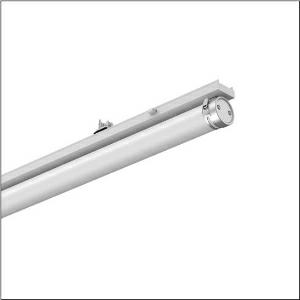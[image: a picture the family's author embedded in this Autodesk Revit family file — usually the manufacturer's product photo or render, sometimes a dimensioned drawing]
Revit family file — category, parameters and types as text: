
# Revit family: monsun_r__31_tube_51ft10nn4a0atr1_e6cc
name_source: partatom
category: Lighting Fixtures
units: mm (PartAtom-declared; Revit-internal decimal feet)

## family parameters
Cut with Voids When Loaded = No
Host = Face
Light Source = No
Part Type = Normal
Room Calculation Point = No
Round Connector Dimension = Use Diameter
Shared = No

## types (1)
- --- (1 x LED, 10000 lm, 58 W, 4000K)
    Apparent Load = 58 VA
    CIE Flux Codes = 42 71 90 91 100
    Color Rendering = 80
    Color Temperature = 4000K
    Default Elevation = 1800 mm
    Description = Monsun® 31 Tube, tubular luminaire, primary optical cover: diffuser, of PMMA, light emission: direct distribution, primary light characteristic: symmetric, LED, rated luminous flux: 10.000lm, luminous efficacy: 172lm/W, light colour: 840, colour temperature: 4000K, control gear: DALI Multilumen, with with 1 terminal, 5-pole, max. 2.5mm², mains connection: 220..240V, AC, 50/60Hz, rated input power: 58W, housing, cylindrical, of PMMA, semi-transparent, matt white, with luminaire and ceiling fastening, V4A, mounting with brackets of stainless steel, length: 1.495mm, diameter: 75mm, end cap, of stainless steel (V4A), protection rating (complete): IP20, protection rating (lamp compartment): IP67/69K, insulation class (complete): insulation class I (protective earthing), certification: CE, UKCA, impact resistance: IK07, permissible operating ambient temperature: -20..+40°C, corresponds to IFS (International Featured Standards) requirements for safety and quality in the food industry, contact your sales advisor before using the luminaires in applications with unclear chemical exposure, large temperature fluctuations or condensation-forming humidity, packaging unit: 1 piece
    Height = 118 mm
    Lamp = 1 x LED
    Lamp Light Flux = 10000 lm
    Lamp Power = 58 W
    Lamp count = 1
    Length = 1495 mm
    Luminous efficacy = 172 lm/W
    Manufacturer = Siteco
    ModVariant = No
    Model = 51FT10NN4A0ATR1
    Mounting Place = Ceiling
    Mounting Type = Pendant
    Number of Poles = 1
    OnlyDefault = Yes
    Power Factor = 1
    Product Name = Monsun® 31 Tube
    Product group = tubular luminaire
    ProductGroupID = 907
    Protection Class = Protection class I
    Protection Degree = IP 20
    RLX_Detail_Level = 1
    RLX_Emergency_Light_Flux = 0 lm
    RLX_Emergency_Type = 0
    RLX_Emergency_Type_DB = No
    RlxData = <blob elided: 32305 chars, md5=eb39772c>
    Socket = socket
    Standby Power = 0 W
    System Light Flux = 10000 lm
    System Power = 58 W
    Type Comments = individual setting: luminous flux: 100 % | (OFF | OFF | ON | OFF) | 350 mA
    Type Image = l_1007227.jpg
    URL = http://relux.com
    VarID = @adj_143370
    Voltage = 0 V
    Weight = 0.00 kg
    Width = 75 mm

## geometry (parser evidence)
native form markers: Blend x4, Sweep x12
no freeform markers — native parametric forms only
